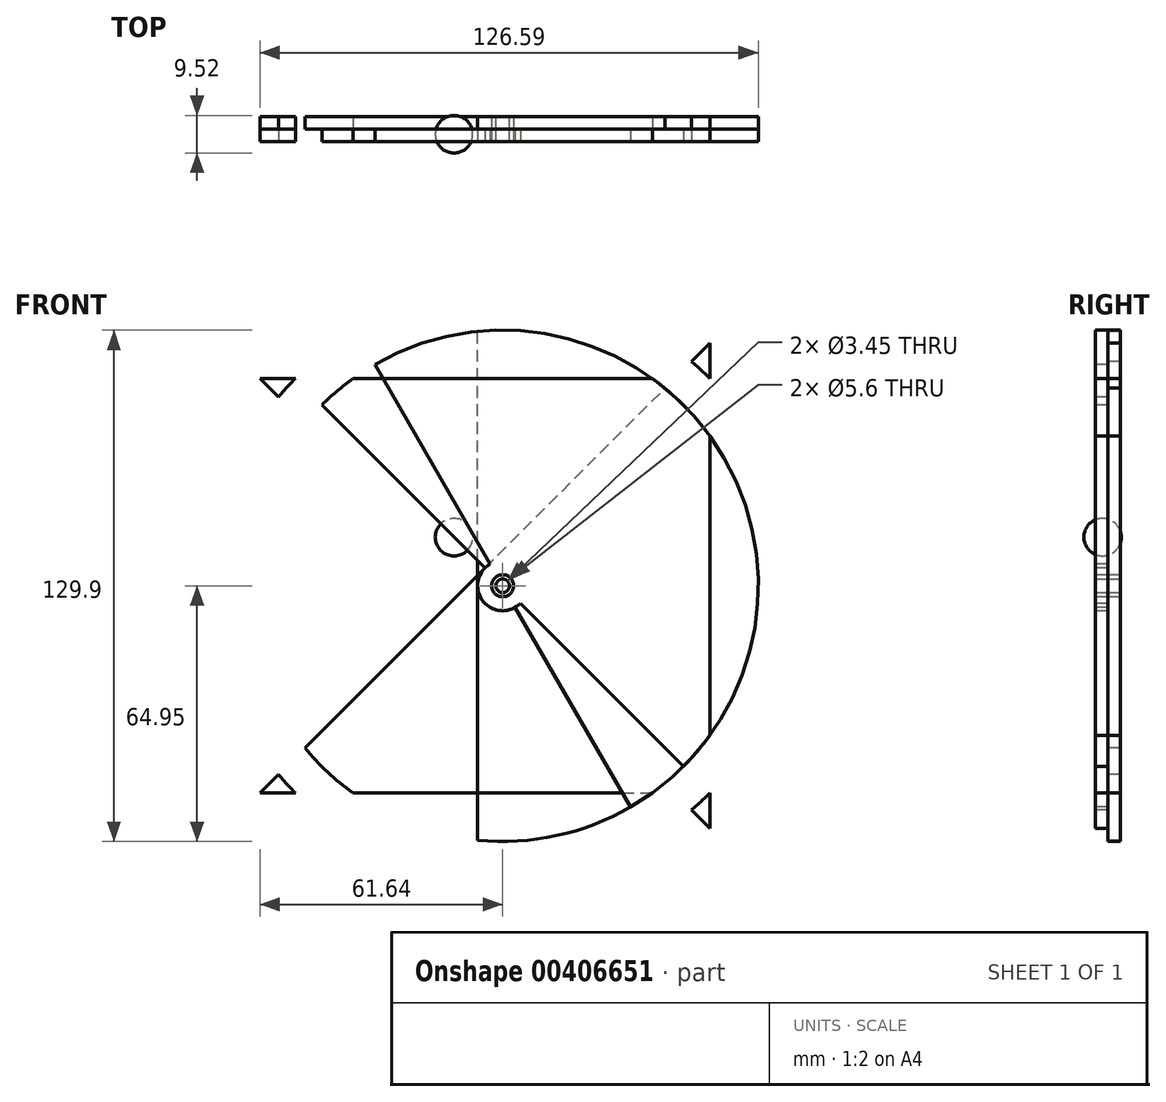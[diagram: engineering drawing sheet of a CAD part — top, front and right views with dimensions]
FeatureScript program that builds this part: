
annotation { "Feature Type Name" : "Feature", "Feature Type Description" : "" }
export const myFeature = defineFeature(function(context is Context, id is Id, definition is map)
    precondition{}
    {
        {
            var Q0;
            Q0=qCreatedBy(makeId("Front.planeOp"),FACE);
            var sketch = newSketch(context, id + "F0", { "sketchPlane" : qUnion([Q0])});
            skLineSegment(sketch, "E0.bottom", {"start": v(-57.15, 57.15) * mm, "end": v(57.15, 57.15) * mm, "construction": true});
            skLineSegment(sketch, "E0.top", {"start": v(-57.15, -57.15) * mm, "end": v(57.15, -57.15) * mm});
            skLineSegment(sketch, "E0.left", {"start": v(-57.15, 57.15) * mm, "end": v(-57.15, -57.15) * mm, "construction": true});
            skLineSegment(sketch, "E0.right", {"start": v(57.15, 57.15) * mm, "end": v(57.15, -57.15) * mm});
            skPoint(sketch, "E0.middle", {"position": v(0, 0) * mm});
            skLineSegment(sketch, "E1", {"start": v(-57.15, -57.15) * mm, "end": v(57.15, 57.15) * mm});
            skLineSegment(sketch, "E2", {"start": v(-57.15, 57.15) * mm, "end": v(57.15, -57.15) * mm, "construction": true});
            skCircle(sketch, "E3", {"center": v(4.5, -4.5) * mm, "radius": 6.35 * mm, "construction": true});
            skCircle(sketch, "E4", {"center": v(4.5, -4.5) * mm, "radius": 1.73 * mm});
            skSolve(sketch);
        }
        {
            var Q0;
            Q0=qSketchRegion(id+"F0",true);
            var Q1;
            Q1=sQuery(id+"F0.wireOp",EDGE,"E0.bottom");
            var Q2;
            Q2=sQuery(id+"F0.wireOp",EDGE,"E0.left");
            extrude(context, id + "F1", {"entities" : qUnion([Q0]), "surfaceEntities" : qUnion([Q1, Q2]), "depth" : 3.17 * mm});
        }
        {
            var Q0;
            Q0=sQuery(id+"F0.wireOp",VERTEX,"E4.center");
            var Q1;
            Q1=qCreatedBy(makeId("Top.planeOp"),FACE);
            cPlane(context, id + "F2", {"entities" : qUnion([Q0, Q1]), "cplaneType" : CPlaneType.PLANE_POINT, "offset" : 25.4 * mm, "width" : 152.4 * mm, "height" : 152.4 * mm});
        }
        {
            var Q0;
            Q0=qCreatedBy(id+"F2.planeOp",FACE);
            var sketch = newSketch(context, id + "F3", { "sketchPlane" : qUnion([Q0])});
            skPoint(sketch, "E5.0", {"position": v(4.5, 0) * mm});
            skLineSegment(sketch, "E6", {"start": v(4.5, 0) * mm, "end": v(4.5, -119.12) * mm});
            skSolve(sketch);
        }
        {
            var Q0;
            Q0=makeQuery(id+"F1.opExtrude","SWEPT_BODY",BODY,{"disambiguationData":[OSD([sQuery(id+"F0.wireOp",EDGE,"E0.top"),sQuery(id+"F0.wireOp",EDGE,"E0.right"),sQuery(id+"F0.wireOp",EDGE,"E1"),sQuery(id+"F0.wireOp",EDGE,"E4")])]});
            var Q1;
            Q1=sQuery(id+"F3.wireOp",EDGE,"E6");
            var Q2;
            Q2=sQuery(id+"F3.wireOp",EDGE,"E6");
            transform(context, id + "F4", {"entities" : qUnion([Q0]), "transformType" : TransformType.ROTATION, "transformAxis" : qUnion([Q2]), "angle" : 90 * degree, "makeCopy" : true});
        }
        {
            var Q0;
            Q0=makeQuery(id+"F4.opPattern","COPY",BODY,{"derivedFrom":makeQuery(id+"F1.opExtrude","SWEPT_BODY",BODY,{"disambiguationData":[OSD([sQuery(id+"F0.wireOp",EDGE,"E0.top"),sQuery(id+"F0.wireOp",EDGE,"E0.right"),sQuery(id+"F0.wireOp",EDGE,"E1"),sQuery(id+"F0.wireOp",EDGE,"E4")])]}),"instanceName":"1"});
            var Q1;
            Q1=sQuery(id+"F3.wireOp",EDGE,"E6");
            transform(context, id + "F5", {"entities" : qUnion([Q0]), "transformType" : TransformType.TRANSLATION_DISTANCE, "transformDirection" : qUnion([Q1]), "distance" : 3.17 * mm, "makeCopy" : false});
        }
        {
            var Q0;
            Q0=makeQuery(id+"F4.opPattern","COPY",FACE,{"derivedFrom":makeQuery(id+"F1.opExtrude","CAP_FACE",FACE,{"disambiguationData":[OSD([sQuery(id+"F0.wireOp",EDGE,"E0.top"),sQuery(id+"F0.wireOp",EDGE,"E0.right"),sQuery(id+"F0.wireOp",EDGE,"E1"),sQuery(id+"F0.wireOp",EDGE,"E4")])],"isStart":false}),"instanceName":"1"});
            var sketch = newSketch(context, id + "F6", { "sketchPlane" : qUnion([Q0])});
            skCircle(sketch, "E7.1", {"center": v(4.5, -4.5) * mm, "radius": 6.35 * mm});
            skSolve(sketch);
        }
        {
            var Q0;
            Q0=qSketchRegion(id+"F6",true);
            extrude(context, id + "F7", {"entities" : qUnion([Q0]), "depth" : 6.35 * mm});
        }
        {
            var Q0;
            Q0=makeQuery(id+"F4.opPattern","COPY",FACE,{"derivedFrom":makeQuery(id+"F1.opExtrude","CAP_FACE",FACE,{"disambiguationData":[OSD([sQuery(id+"F0.wireOp",EDGE,"E0.top"),sQuery(id+"F0.wireOp",EDGE,"E0.right"),sQuery(id+"F0.wireOp",EDGE,"E1"),sQuery(id+"F0.wireOp",EDGE,"E4")])],"isStart":false}),"instanceName":"1"});
            var sketch = newSketch(context, id + "F8", { "sketchPlane" : qUnion([Q0])});
            skLineSegment(sketch, "E8.0", {"start": v(52.47, -61.45) * mm, "end": v(-52.47, 43.49) * mm});
            skArc(sketch, "E9", {"start": v(52.47, -61.45) * mm, "mid": v(57.15, 48.17) * mm, "end": v(-52.47, 43.49) * mm});
            skPoint(sketch, "E10.orphan", {"position": v(-57.15, 48.17) * mm});
            skPoint(sketch, "E11.orphan", {"position": v(57.15, -66.13) * mm});
            skCircle(sketch, "E12", {"center": v(4.5, -4.5) * mm, "radius": 2.8 * mm});
            skSolve(sketch);
        }
        {
            var Q0;
            Q0=qSketchRegion(id+"F8",true);
            extrude(context, id + "F9", {"entities" : qUnion([Q0]), "oppositeDirection" : true, "depth" : 3.17 * mm});
        }
        {
            var Q0;
            Q0=makeQuery(id+"F9.opExtrude","SWEPT_BODY",BODY,{"disambiguationData":[OSD([sQuery(id+"F8.wireOp",EDGE,"E8.0"),sQuery(id+"F8.wireOp",EDGE,"E9"),sQuery(id+"F8.wireOp",EDGE,"E12")])]});
            var Q1;
            Q1=sQuery(id+"F3.wireOp",EDGE,"E6");
            var Q2;
            Q2=sQuery(id+"F3.wireOp",EDGE,"E6");
            transform(context, id + "F10", {"entities" : qUnion([Q0]), "transformType" : TransformType.ROTATION, "transformAxis" : qUnion([Q2]), "angle" : 90 * degree, "oppositeDirection" : true, "makeCopy" : true});
        }
        {
            var Q0;
            Q0=makeQuery(id+"F10.opPattern","COPY",BODY,{"derivedFrom":makeQuery(id+"F9.opExtrude","SWEPT_BODY",BODY,{"disambiguationData":[OSD([sQuery(id+"F8.wireOp",EDGE,"E8.0"),sQuery(id+"F8.wireOp",EDGE,"E9"),sQuery(id+"F8.wireOp",EDGE,"E12")])]}),"instanceName":"1"});
            var Q1;
            Q1=sQuery(id+"F3.wireOp",EDGE,"E6");
            transform(context, id + "F11", {"entities" : qUnion([Q0]), "transformType" : TransformType.TRANSLATION_DISTANCE, "transformDirection" : qUnion([Q1]), "distance" : 3.17 * mm, "oppositeDirection" : true, "makeCopy" : false});
        }
        {
            var Q0;
            Q0=makeQuery(id+"F9.opExtrude","CAP_FACE",FACE,{"disambiguationData":[OSD([sQuery(id+"F8.wireOp",EDGE,"E8.0"),sQuery(id+"F8.wireOp",EDGE,"E9"),sQuery(id+"F8.wireOp",EDGE,"E12")])],"isStart":true});
            var sketch = newSketch(context, id + "F12", { "sketchPlane" : qUnion([Q0])});
            skArc(sketch, "E13.0", {"start": v(52.47, -61.45) * mm, "mid": v(57.15, 48.17) * mm, "end": v(-52.47, 43.49) * mm});
            skLineSegment(sketch, "E13.1", {"start": v(52.47, -61.45) * mm, "end": v(45.7, -54.68) * mm});
            skArc(sketch, "E14.0", {"start": v(45.7, -54.68) * mm, "mid": v(50.41, 41.43) * mm, "end": v(-45.7, 36.72) * mm});
            skLineSegment(sketch, "E15.trimOffspring", {"start": v(-45.7, 36.72) * mm, "end": v(-52.47, 43.49) * mm});
            skSolve(sketch);
        }
        {
            var Q0;
            Q0=qSketchRegion(id+"F12",true);
            extrude(context, id + "F13", {"entities" : qUnion([Q0]), "operationType" : NewBodyOperationType.REMOVE, "endBound" : BoundingType.UP_TO_NEXT, "oppositeDirection" : true, "depth" : 25.4 * mm});
        }
        {
            var Q0;
            Q0=makeQuery(id+"F9.opExtrude","CAP_FACE",FACE,{"disambiguationData":[OSD([sQuery(id+"F8.wireOp",EDGE,"E8.0"),sQuery(id+"F8.wireOp",EDGE,"E9"),sQuery(id+"F8.wireOp",EDGE,"E12")])],"isStart":true});
            var sketch = newSketch(context, id + "F14", { "sketchPlane" : qUnion([Q0])});
            skLineSegment(sketch, "E16.0", {"start": v(45.7, -54.68) * mm, "end": v(-45.7, 36.72) * mm, "construction": true});
            skPoint(sketch, "E16.1", {"position": v(4.5, -4.5) * mm});
            skLineSegment(sketch, "E17", {"start": v(4.5, -4.5) * mm, "end": v(-41.43, 41.43) * mm});
            skLineSegment(sketch, "E18", {"start": v(4.5, -4.5) * mm, "end": v(50.41, 41.43) * mm});
            skLineSegment(sketch, "E19", {"start": v(4.5, -4.5) * mm, "end": v(50.41, -50.41) * mm});
            skSolve(sketch);
        }
        {
            var Q0;
            Q0=makeQuery(id+"F10.opPattern","COPY",FACE,{"derivedFrom":makeQuery(id+"F9.opExtrude","CAP_FACE",FACE,{"disambiguationData":[OSD([sQuery(id+"F8.wireOp",EDGE,"E8.0"),sQuery(id+"F8.wireOp",EDGE,"E9"),sQuery(id+"F8.wireOp",EDGE,"E12")])],"isStart":true}),"instanceName":"1"});
            var sketch = newSketch(context, id + "F15", { "sketchPlane" : qUnion([Q0])});
            skLineSegment(sketch, "E20.0", {"start": v(-52.47, -52.47) * mm, "end": v(52.47, 52.47) * mm});
            skPoint(sketch, "E20.1", {"position": v(4.5, -4.5) * mm});
            skLineSegment(sketch, "E21", {"start": v(-34.7, -43.68) * mm, "end": v(-41.43, -50.41) * mm});
            skLineSegment(sketch, "E22.0", {"start": v(4.5, -4.5) * mm, "end": v(50.41, -50.41) * mm, "construction": true});
            skCircle(sketch, "E23", {"center": v(4.5, -4.5) * mm, "radius": 64.95 * mm, "construction": true});
            skCircle(sketch, "E24.0", {"center": v(4.5, -4.5) * mm, "radius": 55.42 * mm, "construction": true});
            skLineSegment(sketch, "E25.1.0", {"start": v(-27.3, -49.89) * mm, "end": v(-32.76, -57.7) * mm});
            skLineSegment(sketch, "E25.2.0", {"start": v(-18.93, -54.72) * mm, "end": v(-22.96, -63.35) * mm});
            skLineSegment(sketch, "E25.3.0", {"start": v(-9.85, -58.02) * mm, "end": v(-12.32, -67.22) * mm});
            skLineSegment(sketch, "E25.4.0", {"start": v(-0.34, -59.7) * mm, "end": v(-1.17, -69.2) * mm});
            skLineSegment(sketch, "E25.5.0", {"start": v(9.32, -59.7) * mm, "end": v(10.15, -69.2) * mm});
            skLineSegment(sketch, "E25.6.0", {"start": v(18.83, -58.02) * mm, "end": v(21.3, -67.22) * mm});
            skLineSegment(sketch, "E25.7.0", {"start": v(27.91, -54.72) * mm, "end": v(31.94, -63.35) * mm});
            skLineSegment(sketch, "E25.8.0", {"start": v(36.28, -49.89) * mm, "end": v(41.74, -57.7) * mm});
            skLineSegment(sketch, "E25.9.0", {"start": v(43.68, -43.68) * mm, "end": v(50.41, -50.41) * mm});
            skLineSegment(sketch, "E25.anchor1", {"start": v(4.5, -4.5) * mm, "end": v(-41.43, -50.41) * mm, "construction": true});
            skCircle(sketch, "E26.0", {"center": v(4.5, -4.5) * mm, "radius": 60.18 * mm, "construction": true});
            skLineSegment(sketch, "E27.1.0", {"start": v(-38.97, -49.5) * mm, "end": v(-40.63, -51.2) * mm});
            skLineSegment(sketch, "E27.2.0", {"start": v(-33.3, -45.02) * mm, "end": v(-36.56, -48.5) * mm, "construction": true});
            skLineSegment(sketch, "E27.anchor2", {"start": v(4.5, -4.5) * mm, "end": v(-32.76, -57.7) * mm, "construction": true});
            skPoint(sketch, "E28.orphan", {"position": v(-34, -44.36) * mm});
            skCircle(sketch, "E29.0", {"center": v(4.5, -4.5) * mm, "radius": 62.57 * mm, "construction": true});
            skLineSegment(sketch, "E30.2.3.0", {"start": v(-32.6, -45.68) * mm, "end": v(-35.78, -49.22) * mm, "construction": true});
            skLineSegment(sketch, "E30.2.4.0", {"start": v(-31.87, -46.32) * mm, "end": v(-35, -49.91) * mm, "construction": true});
            skLineSegment(sketch, "E30.2.5.0", {"start": v(-34.2, -50.6) * mm, "end": v(-37.26, -54.24) * mm});
            skLineSegment(sketch, "E31.2.6.0", {"start": v(-34.88, -53.11) * mm, "end": v(-36.38, -54.96) * mm});
            skLineSegment(sketch, "E31.2.7.0", {"start": v(-34.03, -53.8) * mm, "end": v(-35.5, -55.67) * mm});
            skLineSegment(sketch, "E31.2.8.0", {"start": v(-33.16, -54.46) * mm, "end": v(-34.6, -56.36) * mm});
            skLineSegment(sketch, "E31.2.9.0", {"start": v(-32.29, -55.1) * mm, "end": v(-33.68, -57.03) * mm});
            skLineSegment(sketch, "E32.trimOffspring", {"start": v(-38.18, -50.25) * mm, "end": v(-39.8, -51.99) * mm});
            skLineSegment(sketch, "E33.trimOffspring", {"start": v(-37.37, -50.99) * mm, "end": v(-38.97, -52.76) * mm});
            skLineSegment(sketch, "E34.trimOffspring", {"start": v(-36.56, -51.7) * mm, "end": v(-38.12, -53.5) * mm});
            skPoint(sketch, "E35.orphan", {"position": v(-31.13, -46.95) * mm});
            skPoint(sketch, "E36.orphan", {"position": v(-30.39, -47.56) * mm});
            skPoint(sketch, "E37.orphan", {"position": v(-29.63, -48.16) * mm});
            skPoint(sketch, "E38.orphan", {"position": v(-28.86, -48.75) * mm});
            skPoint(sketch, "E39.orphan", {"position": v(-28.09, -49.33) * mm});
            skSolve(sketch);
        }
        {
            var Q0;
            Q0=makeQuery(id+"F15.imprint","IMPRINT",FACE,{"disambiguationData":[TD([[makeQuery(id+"F15.imprint","IMPRINT",EDGE,{"derivedFrom":sQuery(id+"F15.wireOp",EDGE,"E20.0")}),-1.0]])]});
            var sketch = newSketch(context, id + "F16", { "sketchPlane" : qUnion([Q0])});
            skPoint(sketch, "E40.0", {"position": v(4.5, -4.5) * mm});
            skLineSegment(sketch, "E41.0", {"start": v(-34.7, -43.68) * mm, "end": v(-41.43, -50.41) * mm});
            skLineSegment(sketch, "E41.1", {"start": v(-38.97, -49.5) * mm, "end": v(-40.63, -51.2) * mm});
            skLineSegment(sketch, "E41.2", {"start": v(-38.18, -50.25) * mm, "end": v(-39.8, -51.99) * mm});
            skLineSegment(sketch, "E41.3", {"start": v(-37.37, -50.99) * mm, "end": v(-38.97, -52.76) * mm});
            skLineSegment(sketch, "E41.4", {"start": v(-36.56, -51.7) * mm, "end": v(-38.12, -53.5) * mm});
            skLineSegment(sketch, "E41.5", {"start": v(-34.2, -50.6) * mm, "end": v(-37.26, -54.24) * mm});
            skLineSegment(sketch, "E41.6", {"start": v(-34.88, -53.11) * mm, "end": v(-36.38, -54.96) * mm});
            skLineSegment(sketch, "E41.7", {"start": v(-34.03, -53.8) * mm, "end": v(-35.5, -55.67) * mm});
            skLineSegment(sketch, "E41.8", {"start": v(-33.16, -54.46) * mm, "end": v(-34.6, -56.36) * mm});
            skLineSegment(sketch, "E41.9", {"start": v(-32.29, -55.1) * mm, "end": v(-33.68, -57.03) * mm});
            skLineSegment(sketch, "E41.10", {"start": v(-27.3, -49.89) * mm, "end": v(-32.76, -57.7) * mm});
            skLineSegment(sketch, "E42.1.0", {"start": v(-18.93, -54.72) * mm, "end": v(-22.96, -63.35) * mm});
            skLineSegment(sketch, "E42.1.2", {"start": v(-30.5, -56.36) * mm, "end": v(-31.83, -58.33) * mm});
            skLineSegment(sketch, "E42.1.3", {"start": v(-29.59, -56.96) * mm, "end": v(-30.88, -58.96) * mm});
            skLineSegment(sketch, "E42.1.4", {"start": v(-28.66, -57.55) * mm, "end": v(-29.93, -59.57) * mm});
            skLineSegment(sketch, "E42.1.5", {"start": v(-27.73, -58.12) * mm, "end": v(-28.96, -60.16) * mm});
            skLineSegment(sketch, "E42.1.6", {"start": v(-25.6, -56.61) * mm, "end": v(-27.98, -60.74) * mm});
            skLineSegment(sketch, "E42.1.7", {"start": v(-25.84, -59.21) * mm, "end": v(-27, -61.3) * mm});
            skLineSegment(sketch, "E42.1.8", {"start": v(-24.88, -59.73) * mm, "end": v(-26, -61.84) * mm});
            skLineSegment(sketch, "E42.1.9", {"start": v(-23.91, -60.24) * mm, "end": v(-25, -62.36) * mm});
            skLineSegment(sketch, "E42.1.10", {"start": v(-22.94, -60.72) * mm, "end": v(-23.98, -62.86) * mm});
            skLineSegment(sketch, "E42.2.0", {"start": v(-9.85, -58.02) * mm, "end": v(-12.32, -67.22) * mm});
            skLineSegment(sketch, "E42.2.1", {"start": v(-18.93, -54.72) * mm, "end": v(-22.96, -63.35) * mm});
            skLineSegment(sketch, "E42.2.2", {"start": v(-20.96, -61.65) * mm, "end": v(-21.93, -63.82) * mm});
            skLineSegment(sketch, "E42.2.3", {"start": v(-19.96, -62.08) * mm, "end": v(-20.89, -64.27) * mm});
            skLineSegment(sketch, "E42.2.4", {"start": v(-18.95, -62.5) * mm, "end": v(-19.84, -64.7) * mm});
            skLineSegment(sketch, "E42.2.5", {"start": v(-17.93, -62.9) * mm, "end": v(-18.78, -65.12) * mm});
            skLineSegment(sketch, "E42.2.6", {"start": v(-16.1, -61.05) * mm, "end": v(-17.72, -65.52) * mm});
            skLineSegment(sketch, "E42.2.7", {"start": v(-15.88, -63.65) * mm, "end": v(-16.65, -65.9) * mm});
            skLineSegment(sketch, "E42.2.8", {"start": v(-14.84, -64) * mm, "end": v(-15.58, -66.26) * mm});
            skLineSegment(sketch, "E42.2.9", {"start": v(-13.8, -64.32) * mm, "end": v(-14.5, -66.6) * mm});
            skLineSegment(sketch, "E42.2.10", {"start": v(-12.76, -64.63) * mm, "end": v(-13.41, -66.92) * mm});
            skLineSegment(sketch, "E42.3.0", {"start": v(-0.34, -59.7) * mm, "end": v(-1.17, -69.2) * mm});
            skLineSegment(sketch, "E42.3.1", {"start": v(-9.85, -58.02) * mm, "end": v(-12.32, -67.22) * mm});
            skLineSegment(sketch, "E42.3.2", {"start": v(-10.65, -65.2) * mm, "end": v(-11.22, -67.5) * mm});
            skLineSegment(sketch, "E42.3.3", {"start": v(-9.58, -65.45) * mm, "end": v(-10.12, -67.77) * mm});
            skLineSegment(sketch, "E42.3.4", {"start": v(-8.52, -65.69) * mm, "end": v(-9.01, -68.02) * mm});
            skLineSegment(sketch, "E42.3.5", {"start": v(-7.45, -65.9) * mm, "end": v(-7.9, -68.24) * mm});
            skLineSegment(sketch, "E42.3.6", {"start": v(-5.96, -63.76) * mm, "end": v(-6.79, -68.45) * mm});
            skLineSegment(sketch, "E42.3.7", {"start": v(-5.3, -66.29) * mm, "end": v(-5.67, -68.64) * mm});
            skLineSegment(sketch, "E42.3.8", {"start": v(-4.22, -66.45) * mm, "end": v(-4.55, -68.8) * mm});
            skLineSegment(sketch, "E42.3.9", {"start": v(-3.13, -66.59) * mm, "end": v(-3.42, -68.95) * mm});
            skLineSegment(sketch, "E42.3.10", {"start": v(-2.05, -66.71) * mm, "end": v(-2.3, -69.08) * mm});
            skLineSegment(sketch, "E42.4.0", {"start": v(9.32, -59.7) * mm, "end": v(10.15, -69.2) * mm});
            skLineSegment(sketch, "E42.4.1", {"start": v(-0.34, -59.7) * mm, "end": v(-1.17, -69.2) * mm});
            skLineSegment(sketch, "E42.4.2", {"start": v(0.13, -66.9) * mm, "end": v(-0.04, -69.28) * mm});
            skLineSegment(sketch, "E42.4.3", {"start": v(1.22, -66.97) * mm, "end": v(1.1, -69.35) * mm});
            skLineSegment(sketch, "E42.4.4", {"start": v(2.3, -67.02) * mm, "end": v(2.22, -69.4) * mm});
            skLineSegment(sketch, "E42.4.5", {"start": v(3.4, -67.05) * mm, "end": v(3.36, -69.43) * mm});
            skLineSegment(sketch, "E42.4.6", {"start": v(4.5, -64.67) * mm, "end": v(4.5, -69.44) * mm});
            skLineSegment(sketch, "E42.4.7", {"start": v(5.58, -67.05) * mm, "end": v(5.62, -69.43) * mm});
            skLineSegment(sketch, "E42.4.8", {"start": v(6.67, -67.02) * mm, "end": v(6.76, -69.4) * mm});
            skLineSegment(sketch, "E42.4.9", {"start": v(7.76, -66.97) * mm, "end": v(7.89, -69.35) * mm});
            skLineSegment(sketch, "E42.4.10", {"start": v(8.85, -66.9) * mm, "end": v(9.02, -69.28) * mm});
            skLineSegment(sketch, "E42.5.0", {"start": v(18.83, -58.02) * mm, "end": v(21.3, -67.22) * mm});
            skLineSegment(sketch, "E42.5.1", {"start": v(9.32, -59.7) * mm, "end": v(10.15, -69.2) * mm});
            skLineSegment(sketch, "E42.5.2", {"start": v(11.03, -66.71) * mm, "end": v(11.28, -69.08) * mm});
            skLineSegment(sketch, "E42.5.3", {"start": v(12.12, -66.59) * mm, "end": v(12.4, -68.95) * mm});
            skLineSegment(sketch, "E42.5.4", {"start": v(13.2, -66.45) * mm, "end": v(13.53, -68.8) * mm});
            skLineSegment(sketch, "E42.5.5", {"start": v(14.28, -66.29) * mm, "end": v(14.65, -68.64) * mm});
            skLineSegment(sketch, "E42.5.6", {"start": v(14.94, -63.76) * mm, "end": v(15.77, -68.45) * mm});
            skLineSegment(sketch, "E42.5.7", {"start": v(16.43, -65.9) * mm, "end": v(16.88, -68.24) * mm});
            skLineSegment(sketch, "E42.5.8", {"start": v(17.5, -65.69) * mm, "end": v(18, -68.02) * mm});
            skLineSegment(sketch, "E42.5.9", {"start": v(18.56, -65.45) * mm, "end": v(19.1, -67.77) * mm});
            skLineSegment(sketch, "E42.5.10", {"start": v(19.63, -65.2) * mm, "end": v(20.2, -67.5) * mm});
            skLineSegment(sketch, "E42.6.0", {"start": v(27.91, -54.72) * mm, "end": v(31.94, -63.35) * mm});
            skLineSegment(sketch, "E42.6.1", {"start": v(18.83, -58.02) * mm, "end": v(21.3, -67.22) * mm});
            skLineSegment(sketch, "E42.6.2", {"start": v(21.74, -64.63) * mm, "end": v(22.4, -66.92) * mm});
            skLineSegment(sketch, "E42.6.3", {"start": v(22.78, -64.32) * mm, "end": v(23.48, -66.6) * mm});
            skLineSegment(sketch, "E42.6.4", {"start": v(23.82, -64) * mm, "end": v(24.56, -66.26) * mm});
            skLineSegment(sketch, "E42.6.5", {"start": v(24.86, -63.65) * mm, "end": v(25.63, -65.9) * mm});
            skLineSegment(sketch, "E42.6.6", {"start": v(25.07, -61.05) * mm, "end": v(26.7, -65.52) * mm});
            skLineSegment(sketch, "E42.6.7", {"start": v(26.91, -62.9) * mm, "end": v(27.77, -65.12) * mm});
            skLineSegment(sketch, "E42.6.8", {"start": v(27.93, -62.5) * mm, "end": v(28.82, -64.7) * mm});
            skLineSegment(sketch, "E42.6.9", {"start": v(28.94, -62.08) * mm, "end": v(29.87, -64.27) * mm});
            skLineSegment(sketch, "E42.6.10", {"start": v(29.94, -61.65) * mm, "end": v(30.9, -63.82) * mm});
            skLineSegment(sketch, "E42.7.0", {"start": v(36.28, -49.89) * mm, "end": v(41.74, -57.7) * mm});
            skLineSegment(sketch, "E42.7.1", {"start": v(27.91, -54.72) * mm, "end": v(31.94, -63.35) * mm});
            skLineSegment(sketch, "E42.7.2", {"start": v(31.92, -60.72) * mm, "end": v(32.96, -62.86) * mm});
            skLineSegment(sketch, "E42.7.3", {"start": v(32.9, -60.24) * mm, "end": v(33.98, -62.36) * mm});
            skLineSegment(sketch, "E42.7.4", {"start": v(33.86, -59.73) * mm, "end": v(34.98, -61.84) * mm});
            skLineSegment(sketch, "E42.7.5", {"start": v(34.82, -59.21) * mm, "end": v(35.98, -61.3) * mm});
            skLineSegment(sketch, "E42.7.6", {"start": v(34.58, -56.61) * mm, "end": v(36.96, -60.74) * mm});
            skLineSegment(sketch, "E42.7.7", {"start": v(36.71, -58.12) * mm, "end": v(37.94, -60.16) * mm});
            skLineSegment(sketch, "E42.7.8", {"start": v(37.65, -57.55) * mm, "end": v(38.9, -59.57) * mm});
            skLineSegment(sketch, "E42.7.9", {"start": v(38.57, -56.96) * mm, "end": v(39.86, -58.96) * mm});
            skLineSegment(sketch, "E42.7.10", {"start": v(39.48, -56.36) * mm, "end": v(40.8, -58.33) * mm});
            skLineSegment(sketch, "E42.8.0", {"start": v(43.68, -43.68) * mm, "end": v(50.41, -50.41) * mm});
            skLineSegment(sketch, "E42.8.1", {"start": v(36.28, -49.89) * mm, "end": v(41.74, -57.7) * mm});
            skLineSegment(sketch, "E42.8.2", {"start": v(41.27, -55.1) * mm, "end": v(42.67, -57.03) * mm});
            skLineSegment(sketch, "E42.8.3", {"start": v(42.14, -54.46) * mm, "end": v(43.58, -56.36) * mm});
            skLineSegment(sketch, "E42.8.4", {"start": v(43, -53.8) * mm, "end": v(44.48, -55.67) * mm});
            skLineSegment(sketch, "E42.8.5", {"start": v(43.86, -53.11) * mm, "end": v(45.36, -54.96) * mm});
            skLineSegment(sketch, "E42.8.6", {"start": v(43.18, -50.6) * mm, "end": v(46.24, -54.24) * mm});
            skLineSegment(sketch, "E42.8.7", {"start": v(45.54, -51.7) * mm, "end": v(47.1, -53.5) * mm});
            skLineSegment(sketch, "E42.8.8", {"start": v(46.35, -50.99) * mm, "end": v(47.95, -52.76) * mm});
            skLineSegment(sketch, "E42.8.9", {"start": v(47.16, -50.25) * mm, "end": v(48.78, -51.99) * mm});
            skLineSegment(sketch, "E42.8.10", {"start": v(47.95, -49.5) * mm, "end": v(49.6, -51.2) * mm});
            skLineSegment(sketch, "E42.anchor1", {"start": v(4.5, -4.5) * mm, "end": v(-41.43, -50.41) * mm, "construction": true});
            skLineSegment(sketch, "E42.anchor2", {"start": v(4.5, -4.5) * mm, "end": v(41.74, -57.7) * mm, "construction": true});
            skLineSegment(sketch, "E43", {"start": v(4.5, -4.5) * mm, "end": v(43.68, -43.68) * mm, "construction": true});
            skLineSegment(sketch, "E44.MirrorCS", {"start": v(56.36, -39.48) * mm, "end": v(58.33, -40.8) * mm});
            skLineSegment(sketch, "E45.MirrorCS", {"start": v(67.02, -2.3) * mm, "end": v(69.4, -2.22) * mm});
            skLineSegment(sketch, "E46.MirrorCS", {"start": v(56.96, -38.57) * mm, "end": v(58.96, -39.86) * mm});
            skLineSegment(sketch, "E47.MirrorCS", {"start": v(66.97, -1.22) * mm, "end": v(69.35, -1.1) * mm});
            skLineSegment(sketch, "E48.MirrorCS", {"start": v(66.9, -8.85) * mm, "end": v(69.28, -9.02) * mm});
            skLineSegment(sketch, "E49.MirrorCS", {"start": v(66.97, -7.76) * mm, "end": v(69.35, -7.89) * mm});
            skLineSegment(sketch, "E50.MirrorCS", {"start": v(54.46, -42.14) * mm, "end": v(56.36, -43.58) * mm});
            skLineSegment(sketch, "E51.MirrorCS", {"start": v(66.59, -12.12) * mm, "end": v(68.95, -12.4) * mm});
            skLineSegment(sketch, "E52.MirrorCS", {"start": v(55.1, -41.27) * mm, "end": v(57.03, -42.67) * mm});
            skLineSegment(sketch, "E53.MirrorCS", {"start": v(66.71, -11.03) * mm, "end": v(69.08, -11.28) * mm});
            skLineSegment(sketch, "E54.MirrorCS", {"start": v(67.05, -3.4) * mm, "end": v(69.43, -3.36) * mm});
            skLineSegment(sketch, "E55.MirrorCS", {"start": v(59.7, -9.32) * mm, "end": v(69.2, -10.15) * mm});
            skLineSegment(sketch, "E56.MirrorCS", {"start": v(54.72, -27.91) * mm, "end": v(63.35, -31.94) * mm});
            skLineSegment(sketch, "E57.MirrorCS", {"start": v(58.02, 9.85) * mm, "end": v(67.22, 12.32) * mm});
            skLineSegment(sketch, "E58.MirrorCS", {"start": v(64.67, -4.5) * mm, "end": v(69.44, -4.5) * mm});
            skLineSegment(sketch, "E59.MirrorCS", {"start": v(61.65, 20.96) * mm, "end": v(63.82, 21.93) * mm});
            skLineSegment(sketch, "E60.MirrorCS", {"start": v(60.72, -31.92) * mm, "end": v(62.86, -32.96) * mm});
            skLineSegment(sketch, "E61.MirrorCS", {"start": v(66.29, -14.28) * mm, "end": v(68.64, -14.65) * mm});
            skLineSegment(sketch, "E62.MirrorCS", {"start": v(61.65, -29.94) * mm, "end": v(63.82, -30.9) * mm});
            skLineSegment(sketch, "E63.MirrorCS", {"start": v(64, -23.82) * mm, "end": v(66.26, -24.56) * mm});
            skLineSegment(sketch, "E64.MirrorCS", {"start": v(54.72, 18.93) * mm, "end": v(63.35, 22.96) * mm});
            skLineSegment(sketch, "E65.MirrorCS", {"start": v(49.89, 27.3) * mm, "end": v(57.7, 32.76) * mm});
            skLineSegment(sketch, "E66.MirrorCS", {"start": v(60.72, 22.94) * mm, "end": v(62.86, 23.98) * mm});
            skLineSegment(sketch, "E67.MirrorCS", {"start": v(66.9, -0.13) * mm, "end": v(69.28, 0.04) * mm});
            skLineSegment(sketch, "E68.MirrorCS", {"start": v(65.9, -16.43) * mm, "end": v(68.24, -16.88) * mm});
            skLineSegment(sketch, "E69.MirrorCS", {"start": v(64.32, -22.78) * mm, "end": v(66.6, -23.48) * mm});
            skLineSegment(sketch, "E70.MirrorCS", {"start": v(66.45, -13.2) * mm, "end": v(68.8, -13.53) * mm});
            skLineSegment(sketch, "E71.MirrorCS", {"start": v(62.08, -28.94) * mm, "end": v(64.27, -29.87) * mm});
            skLineSegment(sketch, "E72.MirrorCS", {"start": v(66.71, 2.05) * mm, "end": v(69.08, 2.3) * mm});
            skLineSegment(sketch, "E73.MirrorCS", {"start": v(67.02, -6.67) * mm, "end": v(69.4, -6.76) * mm});
            skLineSegment(sketch, "E74.MirrorCS", {"start": v(64.63, -21.74) * mm, "end": v(66.92, -22.4) * mm});
            skLineSegment(sketch, "E75.MirrorCS", {"start": v(62.5, -27.93) * mm, "end": v(64.7, -28.82) * mm});
            skLineSegment(sketch, "E76.MirrorCS", {"start": v(66.59, 3.13) * mm, "end": v(68.95, 3.42) * mm});
            skLineSegment(sketch, "E77.MirrorCS", {"start": v(65.2, -19.63) * mm, "end": v(67.5, -20.2) * mm});
            skLineSegment(sketch, "E78.MirrorCS", {"start": v(49.89, -36.28) * mm, "end": v(57.7, -41.74) * mm});
            skLineSegment(sketch, "E79.MirrorCS", {"start": v(59.7, 0.34) * mm, "end": v(69.2, 1.17) * mm});
            skLineSegment(sketch, "E80.MirrorCS", {"start": v(62.08, 19.96) * mm, "end": v(64.27, 20.89) * mm});
            skLineSegment(sketch, "E81.MirrorCS", {"start": v(58.02, -18.83) * mm, "end": v(67.22, -21.3) * mm});
            skLineSegment(sketch, "E82.MirrorCS", {"start": v(67.05, -5.58) * mm, "end": v(69.43, -5.62) * mm});
            skLineSegment(sketch, "E83.MirrorCS", {"start": v(61.05, -25.07) * mm, "end": v(65.52, -26.7) * mm});
            skLineSegment(sketch, "E84.MirrorCS", {"start": v(59.21, 25.84) * mm, "end": v(61.3, 27) * mm});
            skLineSegment(sketch, "E85.MirrorCS", {"start": v(59.21, -34.82) * mm, "end": v(61.3, -35.98) * mm});
            skLineSegment(sketch, "E86.MirrorCS", {"start": v(66.29, 5.3) * mm, "end": v(68.64, 5.67) * mm});
            skLineSegment(sketch, "E87.MirrorCS", {"start": v(63.65, -24.86) * mm, "end": v(65.9, -25.63) * mm});
            skLineSegment(sketch, "E88.MirrorCS", {"start": v(63.76, 5.96) * mm, "end": v(68.45, 6.79) * mm});
            skLineSegment(sketch, "E89.MirrorCS", {"start": v(60.24, -32.9) * mm, "end": v(62.36, -33.98) * mm});
            skLineSegment(sketch, "E90.MirrorCS", {"start": v(64.63, 12.76) * mm, "end": v(66.92, 13.41) * mm});
            skLineSegment(sketch, "E91.MirrorCS", {"start": v(65.45, -18.56) * mm, "end": v(67.77, -19.1) * mm});
            skLineSegment(sketch, "E92.MirrorCS", {"start": v(51.7, -45.54) * mm, "end": v(53.5, -47.1) * mm});
            skLineSegment(sketch, "E93.MirrorCS", {"start": v(65.9, 7.45) * mm, "end": v(68.24, 7.9) * mm});
            skLineSegment(sketch, "E94.MirrorCS", {"start": v(64.32, 13.8) * mm, "end": v(66.6, 14.5) * mm});
            skLineSegment(sketch, "E95.MirrorCS", {"start": v(65.69, -17.5) * mm, "end": v(68.02, -18) * mm});
            skLineSegment(sketch, "E96.MirrorCS", {"start": v(53.8, -43) * mm, "end": v(55.67, -44.48) * mm});
            skLineSegment(sketch, "E97.MirrorCS", {"start": v(61.05, 16.1) * mm, "end": v(65.52, 17.72) * mm});
            skLineSegment(sketch, "E98.MirrorCS", {"start": v(55.1, 32.29) * mm, "end": v(57.03, 33.68) * mm});
            skLineSegment(sketch, "E99.MirrorCS", {"start": v(54.46, 33.16) * mm, "end": v(56.36, 34.6) * mm});
            skLineSegment(sketch, "E100.MirrorCS", {"start": v(53.8, 34.03) * mm, "end": v(55.67, 35.5) * mm});
            skLineSegment(sketch, "E101.MirrorCS", {"start": v(53.11, 34.88) * mm, "end": v(54.96, 36.38) * mm});
            skLineSegment(sketch, "E102.MirrorCS", {"start": v(51.7, 36.56) * mm, "end": v(53.5, 38.12) * mm});
            skLineSegment(sketch, "E103.MirrorCS", {"start": v(50.99, 37.37) * mm, "end": v(52.76, 38.97) * mm});
            skLineSegment(sketch, "E104.MirrorCS", {"start": v(50.25, 38.18) * mm, "end": v(51.99, 39.8) * mm});
            skLineSegment(sketch, "E105.MirrorCS", {"start": v(49.5, 38.97) * mm, "end": v(51.2, 40.63) * mm});
            skLineSegment(sketch, "E106.MirrorCS", {"start": v(57.55, -37.65) * mm, "end": v(59.57, -38.9) * mm});
            skLineSegment(sketch, "E107.MirrorCS", {"start": v(50.6, -43.18) * mm, "end": v(54.24, -46.24) * mm});
            skLineSegment(sketch, "E108.MirrorCS", {"start": v(64, 14.84) * mm, "end": v(66.26, 15.58) * mm});
            skLineSegment(sketch, "E109.MirrorCS", {"start": v(65.69, 8.52) * mm, "end": v(68.02, 9.01) * mm});
            skLineSegment(sketch, "E110.MirrorCS", {"start": v(57.55, 28.66) * mm, "end": v(59.57, 29.93) * mm});
            skLineSegment(sketch, "E111.MirrorCS", {"start": v(56.96, 29.59) * mm, "end": v(58.96, 30.88) * mm});
            skLineSegment(sketch, "E112.MirrorCS", {"start": v(56.36, 30.5) * mm, "end": v(58.33, 31.83) * mm});
            skLineSegment(sketch, "E113.MirrorCS", {"start": v(59.73, -33.86) * mm, "end": v(61.84, -34.98) * mm});
            skLineSegment(sketch, "E114.MirrorCS", {"start": v(62.9, 17.93) * mm, "end": v(65.12, 18.78) * mm});
            skLineSegment(sketch, "E115.MirrorCS", {"start": v(58.12, -36.71) * mm, "end": v(60.16, -37.94) * mm});
            skLineSegment(sketch, "E116.MirrorCS", {"start": v(53.11, -43.86) * mm, "end": v(54.96, -45.36) * mm});
            skLineSegment(sketch, "E117.MirrorCS", {"start": v(60.24, 23.91) * mm, "end": v(62.36, 25) * mm});
            skLineSegment(sketch, "E118.MirrorCS", {"start": v(63.65, 15.88) * mm, "end": v(65.9, 16.65) * mm});
            skLineSegment(sketch, "E119.MirrorCS", {"start": v(65.45, 9.58) * mm, "end": v(67.77, 10.12) * mm});
            skLineSegment(sketch, "E120.MirrorCS", {"start": v(63.76, -14.94) * mm, "end": v(68.45, -15.77) * mm});
            skLineSegment(sketch, "E121.MirrorCS", {"start": v(56.61, 25.6) * mm, "end": v(60.74, 27.98) * mm});
            skLineSegment(sketch, "E122.MirrorCS", {"start": v(62.5, 18.95) * mm, "end": v(64.7, 19.84) * mm});
            skLineSegment(sketch, "E123.MirrorCS", {"start": v(66.45, 4.22) * mm, "end": v(68.8, 4.55) * mm});
            skLineSegment(sketch, "E124.MirrorCS", {"start": v(62.9, -26.91) * mm, "end": v(65.12, -27.77) * mm});
            skLineSegment(sketch, "E125.MirrorCS", {"start": v(65.2, 10.65) * mm, "end": v(67.5, 11.22) * mm});
            skLineSegment(sketch, "E126.MirrorCS", {"start": v(59.73, 24.88) * mm, "end": v(61.84, 26) * mm});
            skLineSegment(sketch, "E127.MirrorCS", {"start": v(56.61, -34.58) * mm, "end": v(60.74, -36.96) * mm});
            skLineSegment(sketch, "E128.MirrorCS", {"start": v(49.5, -47.95) * mm, "end": v(51.2, -49.6) * mm});
            skLineSegment(sketch, "E129.MirrorCS", {"start": v(50.99, -46.35) * mm, "end": v(52.76, -47.95) * mm});
            skLineSegment(sketch, "E130.MirrorCS", {"start": v(58.12, 27.73) * mm, "end": v(60.16, 28.96) * mm});
            skLineSegment(sketch, "E131.MirrorCS", {"start": v(50.6, 34.2) * mm, "end": v(54.24, 37.26) * mm});
            skLineSegment(sketch, "E132.MirrorCS", {"start": v(43.68, 34.7) * mm, "end": v(50.41, 41.43) * mm});
            skLineSegment(sketch, "E133.MirrorCS", {"start": v(50.25, -47.16) * mm, "end": v(51.99, -48.78) * mm});
            skSolve(sketch);
        }
        {
            var Q0;
            Q0=makeQuery(id+"F16.imprint","IMPRINT",FACE,{"disambiguationData":[TD([[makeQuery(id+"F16.imprint","IMPRINT",EDGE,{"derivedFrom":makeQuery(id+"F15.imprint","IMPRINT",EDGE,{"derivedFrom":sQuery(id+"F15.wireOp",EDGE,"E20.0")})}),-1.0]])]});
            var sketch = newSketch(context, id + "F17", { "sketchPlane" : qUnion([Q0])});
            skLineSegment(sketch, "E134.0", {"start": v(-34.7, -43.68) * mm, "end": v(-41.43, -50.41) * mm, "construction": true});
            skPoint(sketch, "E135.0", {"position": v(4.5, -4.5) * mm});
            skLineSegment(sketch, "E136", {"start": v(-41.43, -50.41) * mm, "end": v(4.5, -4.5) * mm});
            skLineSegment(sketch, "E137.1.0", {"start": v(-32.76, -57.7) * mm, "end": v(4.5, -4.5) * mm});
            skLineSegment(sketch, "E137.2.0", {"start": v(-22.96, -63.35) * mm, "end": v(4.5, -4.5) * mm});
            skLineSegment(sketch, "E137.3.0", {"start": v(-12.32, -67.22) * mm, "end": v(4.5, -4.5) * mm});
            skLineSegment(sketch, "E137.4.0", {"start": v(-1.17, -69.2) * mm, "end": v(4.5, -4.5) * mm});
            skLineSegment(sketch, "E137.5.0", {"start": v(10.15, -69.2) * mm, "end": v(4.5, -4.5) * mm});
            skLineSegment(sketch, "E137.6.0", {"start": v(21.3, -67.22) * mm, "end": v(4.5, -4.5) * mm});
            skLineSegment(sketch, "E137.7.0", {"start": v(31.94, -63.35) * mm, "end": v(4.5, -4.5) * mm});
            skLineSegment(sketch, "E137.8.0", {"start": v(41.74, -57.7) * mm, "end": v(4.5, -4.5) * mm});
            skLineSegment(sketch, "E137.9.0", {"start": v(50.41, -50.41) * mm, "end": v(4.5, -4.5) * mm});
            skLineSegment(sketch, "E137.anchor1", {"start": v(4.5, -4.5) * mm, "end": v(-41.43, -50.41) * mm, "construction": true});
            skLineSegment(sketch, "E137.anchor2", {"start": v(4.5, -4.5) * mm, "end": v(50.41, -50.41) * mm, "construction": true});
            skLineSegment(sketch, "E138.MirrorCS", {"start": v(57.7, -41.74) * mm, "end": v(4.5, -4.5) * mm});
            skLineSegment(sketch, "E139.MirrorCS", {"start": v(63.35, -31.94) * mm, "end": v(4.5, -4.5) * mm});
            skLineSegment(sketch, "E140.MirrorCS", {"start": v(67.22, -21.3) * mm, "end": v(4.5, -4.5) * mm});
            skLineSegment(sketch, "E141.MirrorCS", {"start": v(69.2, -10.15) * mm, "end": v(4.5, -4.5) * mm});
            skLineSegment(sketch, "E142.MirrorCS", {"start": v(69.2, 1.17) * mm, "end": v(4.5, -4.5) * mm});
            skLineSegment(sketch, "E143.MirrorCS", {"start": v(67.22, 12.32) * mm, "end": v(4.5, -4.5) * mm});
            skLineSegment(sketch, "E144.MirrorCS", {"start": v(63.35, 22.96) * mm, "end": v(4.5, -4.5) * mm});
            skLineSegment(sketch, "E145.MirrorCS", {"start": v(57.7, 32.76) * mm, "end": v(4.5, -4.5) * mm});
            skLineSegment(sketch, "E146.MirrorCS", {"start": v(4.5, -4.5) * mm, "end": v(50.41, 41.43) * mm});
            skArc(sketch, "E147.0", {"start": v(-52.47, -52.47) * mm, "mid": v(57.15, -57.15) * mm, "end": v(52.47, 52.47) * mm, "construction": true});
            skLineSegment(sketch, "E148.0", {"start": v(-52.47, -52.47) * mm, "end": v(52.47, 52.47) * mm, "construction": true});
            skSolve(sketch);
        }
        {
            var Q0;
            Q0=makeQuery(id+"F17.imprint","IMPRINT",FACE,{"disambiguationData":[TD([[makeQuery(id+"F17.imprint","IMPRINT",EDGE,{"derivedFrom":makeQuery(id+"F16.imprint","IMPRINT",EDGE,{"derivedFrom":makeQuery(id+"F15.imprint","IMPRINT",EDGE,{"derivedFrom":sQuery(id+"F15.wireOp",EDGE,"E20.0")})})}),-1.0]])]});
            var sketch = newSketch(context, id + "F18", { "sketchPlane" : qUnion([Q0])});
            skLineSegment(sketch, "E149.0", {"start": v(-41.43, -50.41) * mm, "end": v(4.5, -4.5) * mm, "construction": true});
            skCircle(sketch, "E150", {"center": v(4.5, -4.5) * mm, "radius": 64.95 * mm, "construction": true});
            skCircle(sketch, "E151", {"center": v(4.5, -4.5) * mm, "radius": 87.6 * mm, "construction": true});
            skLineSegment(sketch, "E152", {"start": v(4.5, -4.5) * mm, "end": v(-51.82, -71.6) * mm});
            skLineSegment(sketch, "E153.1.0", {"start": v(4.5, -4.5) * mm, "end": v(-39.31, -80.36) * mm});
            skLineSegment(sketch, "E153.2.0", {"start": v(4.5, -4.5) * mm, "end": v(-25.47, -86.81) * mm});
            skLineSegment(sketch, "E153.3.0", {"start": v(4.5, -4.5) * mm, "end": v(-10.72, -90.76) * mm});
            skLineSegment(sketch, "E153.4.0", {"start": v(4.5, -4.5) * mm, "end": v(4.5, -92.1) * mm});
            skLineSegment(sketch, "E153.5.0", {"start": v(4.5, -4.5) * mm, "end": v(19.7, -90.76) * mm});
            skLineSegment(sketch, "E153.6.0", {"start": v(4.5, -4.5) * mm, "end": v(34.45, -86.81) * mm});
            skLineSegment(sketch, "E153.7.0", {"start": v(4.5, -4.5) * mm, "end": v(48.3, -80.36) * mm});
            skLineSegment(sketch, "E153.8.0", {"start": v(4.5, -4.5) * mm, "end": v(60.8, -71.6) * mm});
            skLineSegment(sketch, "E153.9.0", {"start": v(4.5, -4.5) * mm, "end": v(71.6, -60.8) * mm});
            skLineSegment(sketch, "E153.anchor1", {"start": v(4.5, -4.5) * mm, "end": v(-51.82, -71.6) * mm, "construction": true});
            skLineSegment(sketch, "E153.anchor2", {"start": v(4.5, -4.5) * mm, "end": v(71.6, -60.8) * mm, "construction": true});
            skLineSegment(sketch, "E154.MirrorCS", {"start": v(4.5, -4.5) * mm, "end": v(80.36, -48.3) * mm});
            skLineSegment(sketch, "E155.MirrorCS", {"start": v(4.5, -4.5) * mm, "end": v(86.81, -34.45) * mm});
            skLineSegment(sketch, "E156.MirrorCS", {"start": v(4.5, -4.5) * mm, "end": v(90.76, -19.7) * mm});
            skLineSegment(sketch, "E157.MirrorCS", {"start": v(4.5, -4.5) * mm, "end": v(92.1, -4.5) * mm});
            skLineSegment(sketch, "E158.MirrorCS", {"start": v(4.5, -4.5) * mm, "end": v(90.76, 10.72) * mm});
            skLineSegment(sketch, "E159.MirrorCS", {"start": v(4.5, -4.5) * mm, "end": v(86.81, 25.47) * mm});
            skLineSegment(sketch, "E160.MirrorCS", {"start": v(4.5, -4.5) * mm, "end": v(80.36, 39.31) * mm});
            skLineSegment(sketch, "E161.MirrorCS", {"start": v(4.5, -4.5) * mm, "end": v(71.6, 51.82) * mm});
            skSolve(sketch);
        }
        {
            var Q0;
            Q0=makeQuery(id+"F17.imprint","IMPRINT",FACE,{"disambiguationData":[TD([[makeQuery(id+"F17.imprint","IMPRINT",EDGE,{"derivedFrom":makeQuery(id+"F16.imprint","IMPRINT",EDGE,{"derivedFrom":makeQuery(id+"F15.imprint","IMPRINT",EDGE,{"derivedFrom":sQuery(id+"F15.wireOp",EDGE,"E20.0")})})}),-1.0]])]});
            var sketch = newSketch(context, id + "F19", { "sketchPlane" : qUnion([Q0])});
            skCircle(sketch, "E162.0", {"center": v(4.5, -4.5) * mm, "radius": 87.6 * mm, "construction": true});
            skLineSegment(sketch, "E163.1", {"start": v(-41.43, -50.41) * mm, "end": v(4.5, -4.5) * mm, "construction": true});
            skLineSegment(sketch, "E164", {"start": v(-57.45, -66.44) * mm, "end": v(-55.66, -64.64) * mm});
            skLineSegment(sketch, "E165.1.0", {"start": v(-56.36, -67.5) * mm, "end": v(-54.6, -65.68) * mm});
            skLineSegment(sketch, "E165.2.0", {"start": v(-55.26, -68.56) * mm, "end": v(-53.52, -66.7) * mm});
            skLineSegment(sketch, "E165.3.0", {"start": v(-54.13, -69.6) * mm, "end": v(-52.43, -67.7) * mm});
            skLineSegment(sketch, "E165.4.0", {"start": v(-52.98, -70.6) * mm, "end": v(-51.32, -68.69) * mm});
            skLineSegment(sketch, "E165.5.0", {"start": v(-51.82, -71.6) * mm, "end": v(-50.19, -69.65) * mm});
            skLineSegment(sketch, "E165.6.0", {"start": v(-50.64, -72.57) * mm, "end": v(-49.04, -70.6) * mm});
            skLineSegment(sketch, "E165.7.0", {"start": v(-49.44, -73.52) * mm, "end": v(-47.88, -71.52) * mm});
            skLineSegment(sketch, "E165.8.0", {"start": v(-48.23, -74.45) * mm, "end": v(-46.7, -72.42) * mm});
            skLineSegment(sketch, "E165.9.0", {"start": v(-47, -75.36) * mm, "end": v(-45.5, -73.3) * mm});
            skLineSegment(sketch, "E165.10.0", {"start": v(-45.76, -76.25) * mm, "end": v(-44.3, -74.17) * mm});
            skLineSegment(sketch, "E165.11.0", {"start": v(-44.5, -77.12) * mm, "end": v(-43.08, -75.01) * mm});
            skLineSegment(sketch, "E165.12.0", {"start": v(-43.22, -77.96) * mm, "end": v(-41.84, -75.83) * mm});
            skLineSegment(sketch, "E165.13.0", {"start": v(-41.93, -78.78) * mm, "end": v(-40.59, -76.63) * mm});
            skLineSegment(sketch, "E165.14.0", {"start": v(-40.63, -79.58) * mm, "end": v(-39.32, -77.4) * mm});
            skLineSegment(sketch, "E165.15.0", {"start": v(-39.31, -80.36) * mm, "end": v(-38.04, -78.16) * mm});
            skLineSegment(sketch, "E165.16.0", {"start": v(-37.98, -81.1) * mm, "end": v(-36.75, -78.89) * mm});
            skLineSegment(sketch, "E165.17.0", {"start": v(-36.64, -81.84) * mm, "end": v(-35.44, -79.6) * mm});
            skLineSegment(sketch, "E165.18.0", {"start": v(-35.28, -82.55) * mm, "end": v(-34.13, -80.28) * mm});
            skLineSegment(sketch, "E165.19.0", {"start": v(-33.91, -83.23) * mm, "end": v(-32.8, -80.94) * mm});
            skLineSegment(sketch, "E165.20.0", {"start": v(-32.53, -83.89) * mm, "end": v(-31.46, -81.58) * mm});
            skLineSegment(sketch, "E165.21.0", {"start": v(-31.14, -84.52) * mm, "end": v(-30.1, -82.2) * mm});
            skLineSegment(sketch, "E165.22.0", {"start": v(-29.74, -85.13) * mm, "end": v(-28.75, -82.8) * mm});
            skLineSegment(sketch, "E165.23.0", {"start": v(-28.33, -85.71) * mm, "end": v(-27.38, -83.36) * mm});
            skLineSegment(sketch, "E165.24.0", {"start": v(-26.9, -86.27) * mm, "end": v(-26, -83.9) * mm});
            skLineSegment(sketch, "E165.25.0", {"start": v(-25.47, -86.81) * mm, "end": v(-24.6, -84.42) * mm});
            skLineSegment(sketch, "E165.26.0", {"start": v(-24.03, -87.32) * mm, "end": v(-23.2, -84.92) * mm});
            skLineSegment(sketch, "E165.27.0", {"start": v(-22.58, -87.8) * mm, "end": v(-21.8, -85.4) * mm});
            skLineSegment(sketch, "E165.28.0", {"start": v(-21.12, -88.27) * mm, "end": v(-20.38, -85.84) * mm});
            skLineSegment(sketch, "E165.29.0", {"start": v(-19.66, -88.7) * mm, "end": v(-18.96, -86.26) * mm});
            skLineSegment(sketch, "E165.30.0", {"start": v(-18.18, -89.1) * mm, "end": v(-17.53, -86.66) * mm});
            skLineSegment(sketch, "E165.31.0", {"start": v(-16.7, -89.5) * mm, "end": v(-16.09, -87.03) * mm});
            skLineSegment(sketch, "E165.32.0", {"start": v(-15.22, -89.85) * mm, "end": v(-14.64, -87.37) * mm});
            skLineSegment(sketch, "E165.33.0", {"start": v(-13.72, -90.18) * mm, "end": v(-13.2, -87.7) * mm});
            skLineSegment(sketch, "E165.34.0", {"start": v(-12.23, -90.48) * mm, "end": v(-11.74, -88) * mm});
            skLineSegment(sketch, "E165.35.0", {"start": v(-10.72, -90.76) * mm, "end": v(-10.28, -88.26) * mm});
            skLineSegment(sketch, "E165.36.0", {"start": v(-9.21, -91.01) * mm, "end": v(-8.82, -88.5) * mm});
            skLineSegment(sketch, "E165.37.0", {"start": v(-7.7, -91.24) * mm, "end": v(-7.35, -88.73) * mm});
            skLineSegment(sketch, "E165.38.0", {"start": v(-6.19, -91.44) * mm, "end": v(-5.88, -88.92) * mm});
            skLineSegment(sketch, "E165.39.0", {"start": v(-4.67, -91.61) * mm, "end": v(-4.4, -89.09) * mm});
            skLineSegment(sketch, "E165.40.0", {"start": v(-3.15, -91.76) * mm, "end": v(-2.92, -89.23) * mm});
            skLineSegment(sketch, "E165.41.0", {"start": v(-1.62, -91.88) * mm, "end": v(-1.44, -89.35) * mm});
            skLineSegment(sketch, "E165.42.0", {"start": v(-0.1, -91.97) * mm, "end": v(0.04, -89.44) * mm});
            skLineSegment(sketch, "E165.43.0", {"start": v(1.43, -92.04) * mm, "end": v(1.52, -89.5) * mm});
            skLineSegment(sketch, "E165.44.0", {"start": v(2.96, -92.08) * mm, "end": v(3, -89.54) * mm});
            skLineSegment(sketch, "E165.45.0", {"start": v(4.5, -92.1) * mm, "end": v(4.5, -89.55) * mm});
            skLineSegment(sketch, "E165.46.0", {"start": v(6.02, -92.08) * mm, "end": v(5.97, -89.54) * mm});
            skLineSegment(sketch, "E165.47.0", {"start": v(7.55, -92.04) * mm, "end": v(7.46, -89.5) * mm});
            skLineSegment(sketch, "E165.48.0", {"start": v(9.07, -91.97) * mm, "end": v(8.94, -89.44) * mm});
            skLineSegment(sketch, "E165.49.0", {"start": v(10.6, -91.88) * mm, "end": v(10.42, -89.35) * mm});
            skLineSegment(sketch, "E165.50.0", {"start": v(12.13, -91.76) * mm, "end": v(11.9, -89.23) * mm});
            skLineSegment(sketch, "E165.51.0", {"start": v(13.65, -91.61) * mm, "end": v(13.38, -89.09) * mm});
            skLineSegment(sketch, "E165.52.0", {"start": v(15.17, -91.44) * mm, "end": v(14.86, -88.92) * mm});
            skLineSegment(sketch, "E165.53.0", {"start": v(16.68, -91.24) * mm, "end": v(16.33, -88.73) * mm});
            skLineSegment(sketch, "E165.54.0", {"start": v(18.2, -91.01) * mm, "end": v(17.8, -88.5) * mm});
            skLineSegment(sketch, "E165.55.0", {"start": v(19.7, -90.76) * mm, "end": v(19.26, -88.26) * mm});
            skLineSegment(sketch, "E165.56.0", {"start": v(21.2, -90.48) * mm, "end": v(20.72, -88) * mm});
            skLineSegment(sketch, "E165.57.0", {"start": v(22.7, -90.18) * mm, "end": v(22.18, -87.7) * mm});
            skLineSegment(sketch, "E165.58.0", {"start": v(24.2, -89.85) * mm, "end": v(23.63, -87.37) * mm});
            skLineSegment(sketch, "E165.59.0", {"start": v(25.68, -89.5) * mm, "end": v(25.07, -87.03) * mm});
            skLineSegment(sketch, "E165.60.0", {"start": v(27.16, -89.1) * mm, "end": v(26.5, -86.66) * mm});
            skLineSegment(sketch, "E165.61.0", {"start": v(28.64, -88.7) * mm, "end": v(27.94, -86.26) * mm});
            skLineSegment(sketch, "E165.62.0", {"start": v(30.1, -88.27) * mm, "end": v(29.36, -85.84) * mm});
            skLineSegment(sketch, "E165.63.0", {"start": v(31.56, -87.8) * mm, "end": v(30.78, -85.4) * mm});
            skLineSegment(sketch, "E165.64.0", {"start": v(33.01, -87.32) * mm, "end": v(32.18, -84.92) * mm});
            skLineSegment(sketch, "E165.65.0", {"start": v(34.45, -86.81) * mm, "end": v(33.58, -84.42) * mm});
            skLineSegment(sketch, "E165.66.0", {"start": v(35.88, -86.27) * mm, "end": v(34.97, -83.9) * mm});
            skLineSegment(sketch, "E165.67.0", {"start": v(37.3, -85.71) * mm, "end": v(36.36, -83.36) * mm});
            skLineSegment(sketch, "E165.68.0", {"start": v(38.72, -85.13) * mm, "end": v(37.73, -82.8) * mm});
            skLineSegment(sketch, "E165.69.0", {"start": v(40.12, -84.52) * mm, "end": v(39.09, -82.2) * mm});
            skLineSegment(sketch, "E165.70.0", {"start": v(41.51, -83.89) * mm, "end": v(40.44, -81.58) * mm});
            skLineSegment(sketch, "E165.71.0", {"start": v(42.9, -83.23) * mm, "end": v(41.78, -80.94) * mm});
            skLineSegment(sketch, "E165.72.0", {"start": v(44.26, -82.55) * mm, "end": v(43.1, -80.28) * mm});
            skLineSegment(sketch, "E165.73.0", {"start": v(45.62, -81.84) * mm, "end": v(44.42, -79.6) * mm});
            skLineSegment(sketch, "E165.74.0", {"start": v(46.96, -81.1) * mm, "end": v(45.73, -78.89) * mm});
            skLineSegment(sketch, "E165.75.0", {"start": v(48.3, -80.36) * mm, "end": v(47.02, -78.16) * mm});
            skLineSegment(sketch, "E165.76.0", {"start": v(49.6, -79.58) * mm, "end": v(48.3, -77.4) * mm});
            skLineSegment(sketch, "E165.77.0", {"start": v(50.91, -78.78) * mm, "end": v(49.57, -76.63) * mm});
            skLineSegment(sketch, "E165.78.0", {"start": v(52.2, -77.96) * mm, "end": v(50.82, -75.83) * mm});
            skLineSegment(sketch, "E165.79.0", {"start": v(53.48, -77.12) * mm, "end": v(52.06, -75.01) * mm});
            skLineSegment(sketch, "E165.anchor1", {"start": v(4.5, -4.5) * mm, "end": v(-57.45, -66.44) * mm, "construction": true});
            skLineSegment(sketch, "E165.anchor2", {"start": v(4.5, -4.5) * mm, "end": v(66.44, -66.44) * mm, "construction": true});
            skLineSegment(sketch, "E166.MirrorCS", {"start": v(66.44, -66.44) * mm, "end": v(64.64, -64.64) * mm});
            skLineSegment(sketch, "E167.1.80.0", {"start": v(54.74, -76.25) * mm, "end": v(53.28, -74.17) * mm});
            skLineSegment(sketch, "E167.1.81.0", {"start": v(55.98, -75.36) * mm, "end": v(54.49, -73.3) * mm});
            skLineSegment(sketch, "E167.1.82.0", {"start": v(57.21, -74.45) * mm, "end": v(55.68, -72.42) * mm});
            skLineSegment(sketch, "E167.1.83.0", {"start": v(58.42, -73.52) * mm, "end": v(56.86, -71.52) * mm});
            skLineSegment(sketch, "E167.1.84.0", {"start": v(59.62, -72.57) * mm, "end": v(58.02, -70.6) * mm});
            skLineSegment(sketch, "E167.1.85.0", {"start": v(60.8, -71.6) * mm, "end": v(59.17, -69.65) * mm});
            skLineSegment(sketch, "E167.1.86.0", {"start": v(61.96, -70.6) * mm, "end": v(60.3, -68.69) * mm});
            skLineSegment(sketch, "E167.1.87.0", {"start": v(63.1, -69.6) * mm, "end": v(61.4, -67.7) * mm});
            skLineSegment(sketch, "E167.1.88.0", {"start": v(64.24, -68.56) * mm, "end": v(62.5, -66.7) * mm});
            skLineSegment(sketch, "E167.1.89.0", {"start": v(65.34, -67.5) * mm, "end": v(63.58, -65.68) * mm});
            skLineSegment(sketch, "E168.MirrorCS", {"start": v(91.61, -13.65) * mm, "end": v(89.09, -13.38) * mm});
            skLineSegment(sketch, "E169.MirrorCS", {"start": v(91.24, -16.68) * mm, "end": v(88.73, -16.33) * mm});
            skLineSegment(sketch, "E170.MirrorCS", {"start": v(90.76, -19.7) * mm, "end": v(88.26, -19.26) * mm});
            skLineSegment(sketch, "E171.MirrorCS", {"start": v(90.18, -22.7) * mm, "end": v(87.7, -22.18) * mm});
            skLineSegment(sketch, "E172.MirrorCS", {"start": v(90.48, -21.2) * mm, "end": v(88, -20.72) * mm});
            skLineSegment(sketch, "E173.MirrorCS", {"start": v(92.08, -2.96) * mm, "end": v(89.54, -3) * mm});
            skLineSegment(sketch, "E174.MirrorCS", {"start": v(91.76, -12.13) * mm, "end": v(89.23, -11.9) * mm});
            skLineSegment(sketch, "E175.MirrorCS", {"start": v(88.7, -28.64) * mm, "end": v(86.26, -27.94) * mm});
            skLineSegment(sketch, "E176.MirrorCS", {"start": v(68.56, 55.26) * mm, "end": v(66.7, 53.52) * mm});
            skLineSegment(sketch, "E177.MirrorCS", {"start": v(67.5, 56.36) * mm, "end": v(65.68, 54.6) * mm});
            skLineSegment(sketch, "E178.MirrorCS", {"start": v(89.5, -25.68) * mm, "end": v(87.03, -25.07) * mm});
            skLineSegment(sketch, "E179.MirrorCS", {"start": v(92.04, -1.43) * mm, "end": v(89.5, -1.52) * mm});
            skLineSegment(sketch, "E180.MirrorCS", {"start": v(91.01, -18.2) * mm, "end": v(88.5, -17.8) * mm});
            skLineSegment(sketch, "E181.MirrorCS", {"start": v(86.27, -35.88) * mm, "end": v(83.9, -34.97) * mm});
            skLineSegment(sketch, "E182.MirrorCS", {"start": v(92.04, -7.55) * mm, "end": v(89.5, -7.46) * mm});
            skLineSegment(sketch, "E183.MirrorCS", {"start": v(87.8, -31.56) * mm, "end": v(85.4, -30.78) * mm});
            skLineSegment(sketch, "E184.MirrorCS", {"start": v(89.85, -24.2) * mm, "end": v(87.37, -23.63) * mm});
            skLineSegment(sketch, "E185.MirrorCS", {"start": v(91.44, -15.17) * mm, "end": v(88.92, -14.86) * mm});
            skLineSegment(sketch, "E186.MirrorCS", {"start": v(66.44, 57.45) * mm, "end": v(64.64, 55.66) * mm});
            skLineSegment(sketch, "E187.MirrorCS", {"start": v(92.08, -6.02) * mm, "end": v(89.54, -5.97) * mm});
            skLineSegment(sketch, "E188.MirrorCS", {"start": v(85.71, -37.3) * mm, "end": v(83.36, -36.36) * mm});
            skLineSegment(sketch, "E189.MirrorCS", {"start": v(91.97, -9.07) * mm, "end": v(89.44, -8.94) * mm});
            skLineSegment(sketch, "E190.MirrorCS", {"start": v(91.88, -10.6) * mm, "end": v(89.35, -10.42) * mm});
            skLineSegment(sketch, "E191.MirrorCS", {"start": v(92.1, -4.5) * mm, "end": v(89.55, -4.5) * mm});
            skLineSegment(sketch, "E192.MirrorCS", {"start": v(87.32, -33.01) * mm, "end": v(84.92, -32.18) * mm});
            skLineSegment(sketch, "E193.MirrorCS", {"start": v(91.44, 6.19) * mm, "end": v(88.92, 5.88) * mm});
            skLineSegment(sketch, "E194.MirrorCS", {"start": v(91.97, 0.1) * mm, "end": v(89.44, -0.04) * mm});
            skLineSegment(sketch, "E195.MirrorCS", {"start": v(89.1, -27.16) * mm, "end": v(86.66, -26.5) * mm});
            skLineSegment(sketch, "E196.MirrorCS", {"start": v(88.27, -30.1) * mm, "end": v(85.84, -29.36) * mm});
            skLineSegment(sketch, "E197.MirrorCS", {"start": v(91.88, 1.62) * mm, "end": v(89.35, 1.44) * mm});
            skLineSegment(sketch, "E198.MirrorCS", {"start": v(86.81, -34.45) * mm, "end": v(84.42, -33.58) * mm});
            skLineSegment(sketch, "E199.MirrorCS", {"start": v(85.13, -38.72) * mm, "end": v(82.8, -37.73) * mm});
            skLineSegment(sketch, "E200.MirrorCS", {"start": v(91.61, 4.67) * mm, "end": v(89.09, 4.4) * mm});
            skLineSegment(sketch, "E201.MirrorCS", {"start": v(91.76, 3.15) * mm, "end": v(89.23, 2.92) * mm});
            skLineSegment(sketch, "E202.MirrorCS", {"start": v(71.6, -60.8) * mm, "end": v(69.65, -59.17) * mm});
            skLineSegment(sketch, "E203.MirrorCS", {"start": v(83.89, -41.51) * mm, "end": v(81.58, -40.44) * mm});
            skLineSegment(sketch, "E204.MirrorCS", {"start": v(78.78, -50.91) * mm, "end": v(76.63, -49.57) * mm});
            skLineSegment(sketch, "E205.MirrorCS", {"start": v(70.6, 52.98) * mm, "end": v(68.69, 51.32) * mm});
            skLineSegment(sketch, "E206.MirrorCS", {"start": v(91.01, 9.21) * mm, "end": v(88.5, 8.82) * mm});
            skLineSegment(sketch, "E207.MirrorCS", {"start": v(72.57, 50.64) * mm, "end": v(70.6, 49.04) * mm});
            skLineSegment(sketch, "E208.MirrorCS", {"start": v(80.36, -48.3) * mm, "end": v(78.16, -47.02) * mm});
            skLineSegment(sketch, "E209.MirrorCS", {"start": v(86.81, 25.47) * mm, "end": v(84.42, 24.6) * mm});
            skLineSegment(sketch, "E210.MirrorCS", {"start": v(84.52, -40.12) * mm, "end": v(82.2, -39.09) * mm});
            skLineSegment(sketch, "E211.MirrorCS", {"start": v(75.36, -55.98) * mm, "end": v(73.3, -54.49) * mm});
            skLineSegment(sketch, "E212.MirrorCS", {"start": v(79.58, 40.63) * mm, "end": v(77.4, 39.32) * mm});
            skLineSegment(sketch, "E213.MirrorCS", {"start": v(69.6, -63.1) * mm, "end": v(67.7, -61.4) * mm});
            skLineSegment(sketch, "E214.MirrorCS", {"start": v(83.89, 32.53) * mm, "end": v(81.58, 31.46) * mm});
            skLineSegment(sketch, "E215.MirrorCS", {"start": v(76.25, -54.74) * mm, "end": v(74.17, -53.28) * mm});
            skLineSegment(sketch, "E216.MirrorCS", {"start": v(90.48, 12.23) * mm, "end": v(88, 11.74) * mm});
            skLineSegment(sketch, "E217.MirrorCS", {"start": v(87.8, 22.58) * mm, "end": v(85.4, 21.8) * mm});
            skLineSegment(sketch, "E218.MirrorCS", {"start": v(81.84, -45.62) * mm, "end": v(79.6, -44.42) * mm});
            skLineSegment(sketch, "E219.MirrorCS", {"start": v(82.55, 35.28) * mm, "end": v(80.28, 34.13) * mm});
            skLineSegment(sketch, "E220.MirrorCS", {"start": v(85.71, 28.33) * mm, "end": v(83.36, 27.38) * mm});
            skLineSegment(sketch, "E221.MirrorCS", {"start": v(86.27, 26.9) * mm, "end": v(83.9, 26) * mm});
            skLineSegment(sketch, "E222.MirrorCS", {"start": v(82.55, -44.26) * mm, "end": v(80.28, -43.1) * mm});
            skLineSegment(sketch, "E223.MirrorCS", {"start": v(90.18, 13.72) * mm, "end": v(87.7, 13.2) * mm});
            skLineSegment(sketch, "E224.MirrorCS", {"start": v(77.96, -52.2) * mm, "end": v(75.83, -50.82) * mm});
            skLineSegment(sketch, "E225.MirrorCS", {"start": v(91.24, 7.7) * mm, "end": v(88.73, 7.35) * mm});
            skLineSegment(sketch, "E226.MirrorCS", {"start": v(90.76, 10.72) * mm, "end": v(88.26, 10.28) * mm});
            skLineSegment(sketch, "E227.MirrorCS", {"start": v(88.27, 21.12) * mm, "end": v(85.84, 20.38) * mm});
            skLineSegment(sketch, "E228.MirrorCS", {"start": v(83.23, 33.91) * mm, "end": v(80.94, 32.8) * mm});
            skLineSegment(sketch, "E229.MirrorCS", {"start": v(80.36, 39.31) * mm, "end": v(78.16, 38.04) * mm});
            skLineSegment(sketch, "E230.MirrorCS", {"start": v(78.78, 41.93) * mm, "end": v(76.63, 40.59) * mm});
            skLineSegment(sketch, "E231.MirrorCS", {"start": v(74.45, 48.23) * mm, "end": v(72.42, 46.7) * mm});
            skLineSegment(sketch, "E232.MirrorCS", {"start": v(68.56, -64.24) * mm, "end": v(66.7, -62.5) * mm});
            skLineSegment(sketch, "E233.MirrorCS", {"start": v(79.58, -49.6) * mm, "end": v(77.4, -48.3) * mm});
            skLineSegment(sketch, "E234.MirrorCS", {"start": v(81.1, 37.98) * mm, "end": v(78.89, 36.75) * mm});
            skLineSegment(sketch, "E235.MirrorCS", {"start": v(83.23, -42.9) * mm, "end": v(80.94, -41.78) * mm});
            skLineSegment(sketch, "E236.MirrorCS", {"start": v(73.52, -58.42) * mm, "end": v(71.52, -56.86) * mm});
            skLineSegment(sketch, "E237.MirrorCS", {"start": v(81.1, -46.96) * mm, "end": v(78.89, -45.73) * mm});
            skLineSegment(sketch, "E238.MirrorCS", {"start": v(69.6, 54.13) * mm, "end": v(67.7, 52.43) * mm});
            skLineSegment(sketch, "E239.MirrorCS", {"start": v(74.45, -57.21) * mm, "end": v(72.42, -55.68) * mm});
            skLineSegment(sketch, "E240.MirrorCS", {"start": v(85.13, 29.74) * mm, "end": v(82.8, 28.75) * mm});
            skLineSegment(sketch, "E241.MirrorCS", {"start": v(70.6, -61.96) * mm, "end": v(68.69, -60.3) * mm});
            skLineSegment(sketch, "E242.MirrorCS", {"start": v(77.12, 44.5) * mm, "end": v(75.01, 43.08) * mm});
            skLineSegment(sketch, "E243.MirrorCS", {"start": v(77.12, -53.48) * mm, "end": v(75.01, -52.06) * mm});
            skLineSegment(sketch, "E244.MirrorCS", {"start": v(75.36, 47) * mm, "end": v(73.3, 45.5) * mm});
            skLineSegment(sketch, "E245.MirrorCS", {"start": v(71.6, 51.82) * mm, "end": v(69.65, 50.19) * mm});
            skLineSegment(sketch, "E246.MirrorCS", {"start": v(84.52, 31.14) * mm, "end": v(82.2, 30.1) * mm});
            skLineSegment(sketch, "E247.MirrorCS", {"start": v(81.84, 36.64) * mm, "end": v(79.6, 35.44) * mm});
            skLineSegment(sketch, "E248.MirrorCS", {"start": v(73.52, 49.44) * mm, "end": v(71.52, 47.88) * mm});
            skLineSegment(sketch, "E249.MirrorCS", {"start": v(72.57, -59.62) * mm, "end": v(70.6, -58.02) * mm});
            skLineSegment(sketch, "E250.MirrorCS", {"start": v(87.32, 24.03) * mm, "end": v(84.92, 23.2) * mm});
            skLineSegment(sketch, "E251.MirrorCS", {"start": v(88.7, 19.66) * mm, "end": v(86.26, 18.96) * mm});
            skLineSegment(sketch, "E252.MirrorCS", {"start": v(67.5, -65.34) * mm, "end": v(65.68, -63.58) * mm});
            skLineSegment(sketch, "E253.MirrorCS", {"start": v(89.85, 15.22) * mm, "end": v(87.37, 14.64) * mm});
            skLineSegment(sketch, "E254.MirrorCS", {"start": v(89.5, 16.7) * mm, "end": v(87.03, 16.09) * mm});
            skLineSegment(sketch, "E255.MirrorCS", {"start": v(77.96, 43.22) * mm, "end": v(75.83, 41.84) * mm});
            skLineSegment(sketch, "E256.MirrorCS", {"start": v(76.25, 45.76) * mm, "end": v(74.17, 44.3) * mm});
            skLineSegment(sketch, "E257.MirrorCS", {"start": v(89.1, 18.18) * mm, "end": v(86.66, 17.53) * mm});
            skSolve(sketch);
        }
        {
            var Q0;
            Q0=makeQuery(id+"F17.imprint","IMPRINT",FACE,{"disambiguationData":[TD([[makeQuery(id+"F17.imprint","IMPRINT",EDGE,{"derivedFrom":makeQuery(id+"F16.imprint","IMPRINT",EDGE,{"derivedFrom":makeQuery(id+"F15.imprint","IMPRINT",EDGE,{"derivedFrom":sQuery(id+"F15.wireOp",EDGE,"E20.0")})})}),-1.0]])]});
            var sketch = newSketch(context, id + "F20", { "sketchPlane" : qUnion([Q0])});
            skLineSegment(sketch, "E258.0", {"start": v(-52.47, -52.47) * mm, "end": v(-45.7, -45.7) * mm});
            skArc(sketch, "E259.0", {"start": v(45.7, -54.68) * mm, "mid": v(69.44, -4.5) * mm, "end": v(45.7, 45.7) * mm, "construction": true});
            skArc(sketch, "E260", {"start": v(-45.7, -45.7) * mm, "mid": v(50.41, -50.41) * mm, "end": v(45.7, 45.7) * mm});
            skPoint(sketch, "E261.orphan", {"position": v(-45.7, 36.72) * mm});
            skLineSegment(sketch, "E262.trimOffspring", {"start": v(45.7, 45.7) * mm, "end": v(52.47, 52.47) * mm});
            skArc(sketch, "E263.0", {"start": v(-52.47, -52.47) * mm, "mid": v(57.15, -57.15) * mm, "end": v(52.47, 52.47) * mm});
            skSolve(sketch);
        }
        {
            var Q0;
            Q0=qSketchRegion(id+"F20",true);
            extrude(context, id + "F21", {"entities" : qUnion([Q0]), "operationType" : NewBodyOperationType.REMOVE, "oppositeDirection" : true, "depth" : 3.17 * mm});
        }
        {
            var Q0;
            Q0=makeQuery(id+"F9.opExtrude","CAP_FACE",FACE,{"disambiguationData":[OSD([sQuery(id+"F8.wireOp",EDGE,"E8.0"),sQuery(id+"F8.wireOp",EDGE,"E9"),sQuery(id+"F8.wireOp",EDGE,"E12")])],"isStart":true});
            var sketch = newSketch(context, id + "F22", { "sketchPlane" : qUnion([Q0])});
            skCircle(sketch, "E264.0", {"center": v(4.5, -4.5) * mm, "radius": 2.8 * mm, "construction": true});
            skLineSegment(sketch, "E264.1", {"start": v(45.7, -54.68) * mm, "end": v(-45.7, 36.72) * mm});
            skArc(sketch, "E265", {"start": v(0, 0) * mm, "mid": v(0, -8.98) * mm, "end": v(8.98, -8.98) * mm});
            skLineSegment(sketch, "E266", {"start": v(-41.43, 41.43) * mm, "end": v(0, 0) * mm});
            skArc(sketch, "E267.0", {"start": v(45.7, -54.68) * mm, "mid": v(48.11, -52.6) * mm, "end": v(50.41, -50.41) * mm});
            skArc(sketch, "E268.trimOffspring", {"start": v(-41.43, 41.43) * mm, "mid": v(-43.63, 39.13) * mm, "end": v(-45.7, 36.72) * mm});
            skLineSegment(sketch, "E269.trimOffspring", {"start": v(8.98, -8.98) * mm, "end": v(50.41, -50.41) * mm});
            skSolve(sketch);
        }
        {
            var Q0;
            Q0 = qSketchRegion(id + "F22", true);
            extrude(context, id + "F23", {"entities" : qUnion([Q0]), "operationType" : NewBodyOperationType.REMOVE, "endBound" : BoundingType.UP_TO_NEXT, "oppositeDirection" : true, "depth" : 25.4 * mm});
        }
        {
            var Q0;
            Q0=makeQuery(id+"F7.opExtrude","SWEPT_BODY",BODY,{"disambiguationData":[OSD([sQuery(id+"F6.wireOp",EDGE,"E7.1")])]});
            var Q1;
            Q1=makeQuery(id+"F9.opExtrude","SWEPT_BODY",BODY,{"disambiguationData":[OSD([sQuery(id+"F8.wireOp",EDGE,"E8.0"),sQuery(id+"F8.wireOp",EDGE,"E9"),sQuery(id+"F8.wireOp",EDGE,"E12")])]});
            var Q2;
            Q2=makeQuery(id+"F10.opPattern","COPY",BODY,{"derivedFrom":makeQuery(id+"F9.opExtrude","SWEPT_BODY",BODY,{"disambiguationData":[OSD([sQuery(id+"F8.wireOp",EDGE,"E8.0"),sQuery(id+"F8.wireOp",EDGE,"E9"),sQuery(id+"F8.wireOp",EDGE,"E12")])]}),"instanceName":"1"});
            var Q3;
            Q3=sQuery(id+"F3.wireOp",EDGE,"E6");
            transform(context, id + "F24", {"entities" : qUnion([Q0, Q1, Q2]), "transformType" : TransformType.ROTATION, "transformAxis" : qUnion([Q3]), "angle" : 45 * degree, "makeCopy" : false});
        }
        {
            var Q0;
            Q0=makeQuery(id+"F7.opExtrude","SWEPT_BODY",BODY,{"disambiguationData":[OSD([sQuery(id+"F6.wireOp",EDGE,"E7.1")])]});
            deleteBodies(context, id + "F25", {"entities" : qUnion([Q0])});
        }
        {
            var Q0;
            Q0=makeQuery(id+"F23.boolean.opBoolean","COPY",FACE,{"derivedFrom":makeQuery(id+"F23.opExtrude","SWEPT_FACE",FACE,{"disambiguationData":[OSD([sQuery(id+"F22.wireOp",EDGE,"E269.trimOffspring")])]})});
            var sketch = newSketch(context, id + "F26", { "sketchPlane" : qUnion([Q0])});
            skLineSegment(sketch, "E270.0", {"start": v(-1.86, 6.35) * mm, "end": v(10.84, 6.35) * mm, "construction": true});
            skArc(sketch, "E271", {"start": v(4.5, 6.35) * mm, "mid": v(9.25, 11.11) * mm, "end": v(4.5, 15.88) * mm});
            skPoint(sketch, "E271.centerSnap0", {"position": v(4.5, 6.35) * mm});
            skLineSegment(sketch, "E272", {"start": v(4.5, 6.35) * mm, "end": v(4.5, 15.88) * mm});
            skSolve(sketch);
        }
        {
            var Q0;
            Q0 = qSketchRegion(id + "F26", true);
            var Q1;
            Q1=sQuery(id+"F26.wireOp",EDGE,"E272");
            revolve(context, id + "F27", {"entities" : qUnion([Q0]), "axis" : qUnion([Q1]), "revolveType" : RevolveType.FULL});
        }
        {
            var Q0;
            Q0=makeQuery(id+"F9.opExtrude","SWEPT_BODY",BODY,{"disambiguationData":[OSD([sQuery(id+"F8.wireOp",EDGE,"E8.0"),sQuery(id+"F8.wireOp",EDGE,"E9"),sQuery(id+"F8.wireOp",EDGE,"E12")])]});
            var Q1;
            Q1=sQuery(id+"F3.wireOp",EDGE,"E6");
            transform(context, id + "F28", {"entities" : qUnion([Q0]), "transformType" : TransformType.ROTATION, "transformAxis" : qUnion([Q1]), "angle" : 270 * degree, "makeCopy" : false});
        }
        {
            var Q0;
            Q0=makeQuery(id+"F9.opExtrude","SWEPT_BODY",BODY,{"disambiguationData":[OSD([sQuery(id+"F8.wireOp",EDGE,"E8.0"),sQuery(id+"F8.wireOp",EDGE,"E9"),sQuery(id+"F8.wireOp",EDGE,"E12")])]});
            var Q1;
            Q1=sQuery(id+"F3.wireOp",EDGE,"E6");
            var Q2;
            Q2=sQuery(id+"F3.wireOp",EDGE,"E6");
            transform(context, id + "F29", {"entities" : qUnion([Q0]), "transformType" : TransformType.ROTATION, "transformAxis" : qUnion([Q2]), "angle" : 30 * degree, "makeCopy" : false});
        }
    });
